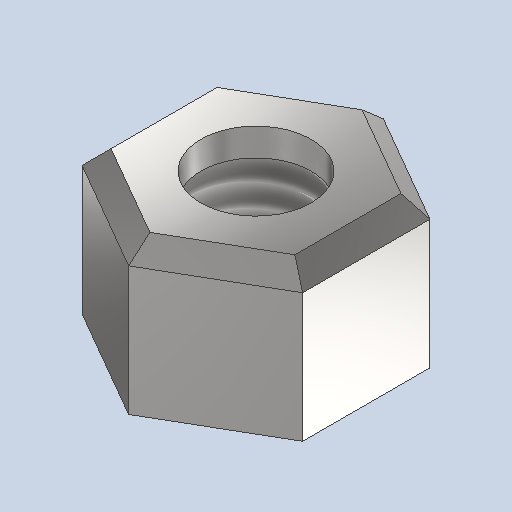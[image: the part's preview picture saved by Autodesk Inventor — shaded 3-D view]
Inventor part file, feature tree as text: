
AUTODESK INVENTOR PART (.ipt)
format: ipt  version: 2025.1 (Build 291241000, 241)  size: 142,336 bytes
history: native  units: mm
features: sketch x3, hole x2, extrude x1, chamfer x1
ambient origin geometry x8: Origin, YZ Plane, XZ Plane, XY Plane, X Axis, Y Axis, Z Axis, Center Point
bodies: Solid1 (feature_tree)
feature tree (7):
  extrude  "Extrusion1"  Depth=8.0mm TaperAngle=0.0deg
  chamfer  "Chamfer1"  Distance=1.0mm Angle=45.0deg
  hole  "Hole1"  [1 undecoded]
  hole  "Hole2"  [1 undecoded]
  sketch  "Sketch1"  dims[d0=12.0mm d1=8.0mm d2=0.0mm d3=1.0mm d4=2.0mm d5=45.0deg]
  sketch  "Sketch2"  dims[d6=6.0mm d7=6.0mm d8=4.0mm d9=2.0mm d10=90.0deg d11=1.5mm d12=0.0mm]
  sketch  "Sketch3"  dims[d13=6.647mm d14=6.5mm d15=4.0mm d16=2.0mm d17=90.0deg d18=6.5mm d19=0.0mm]
note: 2 required parameter values undecoded (feature->parameter linkage not recoverable at this tier; creation-order binding heuristic only, values carry confidence <= 0.55)
